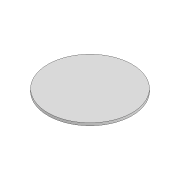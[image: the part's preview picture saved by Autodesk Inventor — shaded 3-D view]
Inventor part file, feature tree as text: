
AUTODESK INVENTOR PART (.ipt)
format: ipt  version: 2022 (Build 260153000, 153)  size: 74,752 bytes
history: native  units: mm
features: extrude x1, sketch x1
ambient origin geometry x8: Origin, YZ Plane, XZ Plane, XY Plane, X Axis, Y Axis, Z Axis, Center Point
bodies: Solid1 (feature_tree)
feature tree (2):
  extrude  "Extrusion1"  Depth=10.0mm TaperAngle=0.0deg
  sketch  "Sketch1"  dims[d0=331.5mm d1=10.0mm d2=0.0mm]
